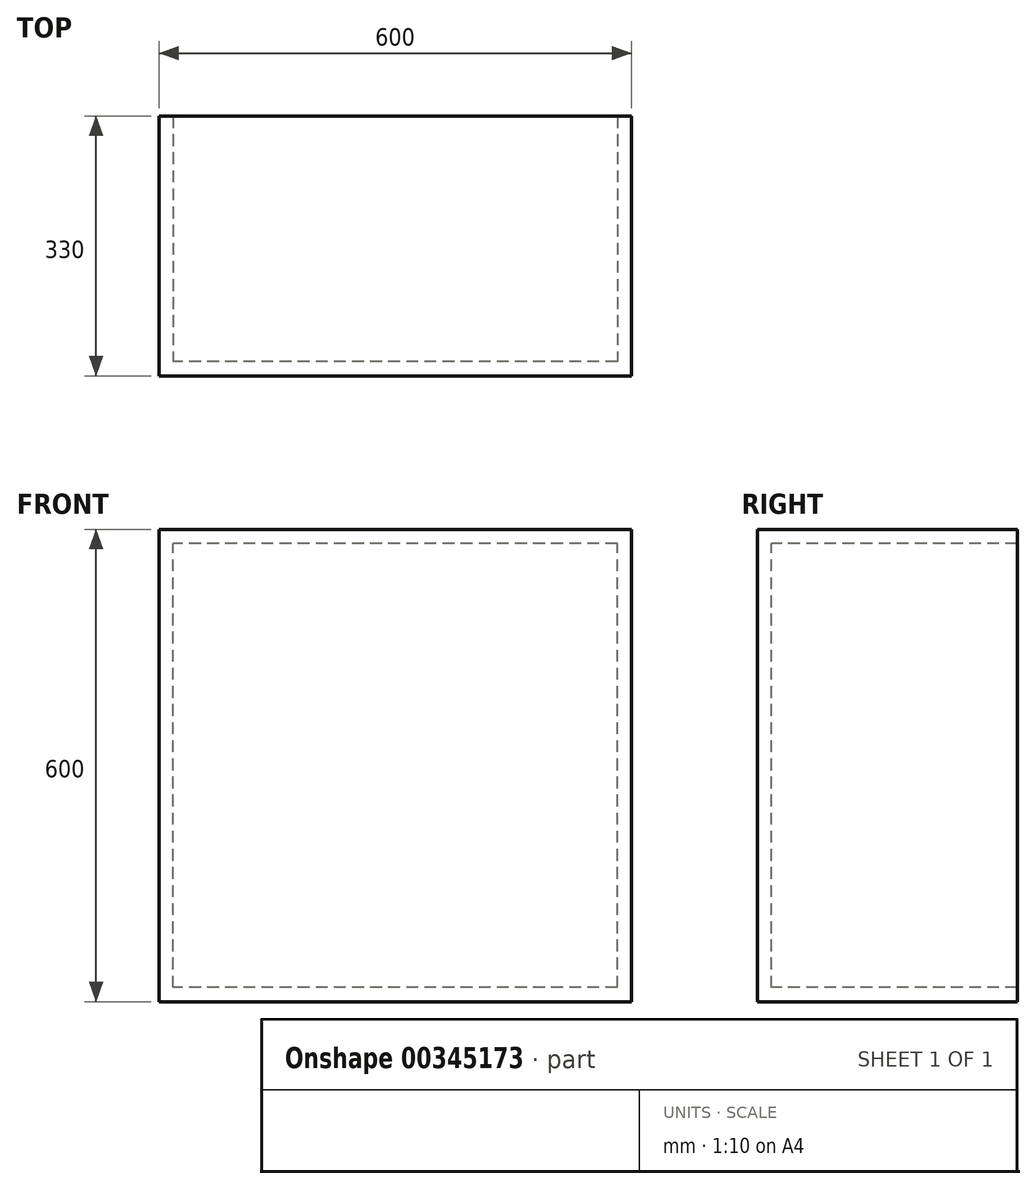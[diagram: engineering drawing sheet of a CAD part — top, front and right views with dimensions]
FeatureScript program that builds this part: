
annotation { "Feature Type Name" : "Feature", "Feature Type Description" : "" }
export const myFeature = defineFeature(function(context is Context, id is Id, definition is map)
    precondition{}
    {
        {
            var Q0;
            Q0=qCreatedBy(makeId("Front.planeOp"),FACE);
            var sketch = newSketch(context, id + "F0", { "sketchPlane" : qUnion([Q0])});
            skLineSegment(sketch, "E0.bottom", {"start": v(0, 0) * mm, "end": v(-52.5, 0) * mm});
            skLineSegment(sketch, "E0.top", {"start": v(0, 35.38) * mm, "end": v(-52.5, 35.38) * mm});
            skLineSegment(sketch, "E0.left", {"start": v(0, 0) * mm, "end": v(0, 35.38) * mm});
            skLineSegment(sketch, "E0.right", {"start": v(-52.5, 0) * mm, "end": v(-52.5, 35.38) * mm});
            skSolve(sketch);
        }
        {
            var Q0;
            Q0=makeQuery(id+"F0.imprint","IMPRINT",FACE,{"disambiguationData":[TD([[makeQuery(id+"F0.imprint","IMPRINT",EDGE,{"derivedFrom":sQuery(id+"F0.wireOp",EDGE,"E0.bottom")}),-1.0]])]});
            extrude(context, id + "F1", {"entities" : qUnion([Q0]), "oppositeDirection" : true, "depth" : 330 * mm});
        }
        {
            var Q0;
            Q0=makeQuery(id+"F1.opExtrude","SWEPT_FACE",FACE,{"disambiguationData":[OSD([sQuery(id+"F0.wireOp",EDGE,"E0.bottom")])]});
            extrude(context, id + "F2", {"entities" : qUnion([Q0]), "operationType" : NewBodyOperationType.ADD, "oppositeDirection" : true, "depth" : 600 * mm});
        }
        {
            var Q0;
            {var subQ0=sQuery(id+"F0.wireOp",EDGE,"E0.left");Q0=makeQuery(id+"F2.boolean.opBoolean","MERGE",FACE,{"derivedFrom":[makeQuery(id+"F1.opExtrude","SWEPT_FACE",FACE,{"disambiguationData":[OSD([subQ0])]}),makeQuery(id+"F2.opExtrude","SWEPT_FACE",FACE,{"disambiguationData":[OSD([sQuery(id+"F0.wireOp",EDGE,"E0.bottom"),subQ0])]})]});}
            extrude(context, id + "F3", {"entities" : qUnion([Q0]), "operationType" : NewBodyOperationType.ADD, "oppositeDirection" : true, "depth" : 600 * mm});
        }
        {
            var Q0;
            {var subQ0=sQuery(id+"F0.wireOp",EDGE,"E0.left");var subQ1=sQuery(id+"F0.wireOp",EDGE,"E0.bottom");Q0=makeQuery(id+"F3.boolean.opBoolean","MERGE",FACE,{"derivedFrom":[makeQuery(id+"F2.boolean.opBoolean","MERGE",FACE,{"derivedFrom":[makeQuery(id+"F1.opExtrude","CAP_FACE",FACE,{"disambiguationData":[OSD([subQ1,sQuery(id+"F0.wireOp",EDGE,"E0.top"),subQ0,sQuery(id+"F0.wireOp",EDGE,"E0.right")])],"isStart":false}),makeQuery(id+"F2.opExtrude","SWEPT_FACE",FACE,{"disambiguationData":[OSD([subQ1]),TDD([makeQuery(id+"F1.opExtrude","CAP_EDGE",EDGE,{"disambiguationData":[OSD([subQ1])],"isStart":false})])]})]}),makeQuery(id+"F3.opExtrude","SWEPT_FACE",FACE,{"disambiguationData":[OSD([subQ1,subQ0]),TDD([makeQuery(id+"F2.boolean.opBoolean","MERGE",EDGE,{"derivedFrom":[makeQuery(id+"F1.opExtrude","CAP_EDGE",EDGE,{"disambiguationData":[OSD([subQ0])],"isStart":false}),makeQuery(id+"F2.opExtrude","SWEPT_EDGE",EDGE,{"disambiguationData":[OSD([subQ1,subQ0]),TDD([makeQuery(id+"F1.opExtrude","CAP_VERTEX",VERTEX,{"disambiguationData":[OSD([subQ1,subQ0])],"isStart":false})])]})]})])]})]});}
            shell(context, id + "F4", {"entities" : qUnion([Q0]), "thickness" : 18 * mm});
        }
    });
